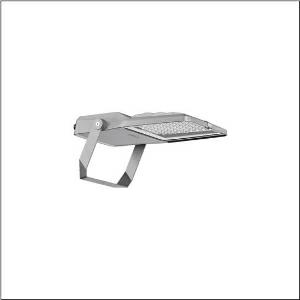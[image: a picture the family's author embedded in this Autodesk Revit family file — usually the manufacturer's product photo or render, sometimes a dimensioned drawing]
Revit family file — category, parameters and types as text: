
# Revit family: floodlight_fl_21_mini___pl43_5xa7775c2a1a_0644
name_source: partatom
category: Lighting Fixtures
units: mm (PartAtom-declared; Revit-internal decimal feet)

## family parameters
Cut with Voids When Loaded = No
Host = Face
Light Source = No
Part Type = Normal
Room Calculation Point = No
Round Connector Dimension = Use Diameter
Shared = No

## types (1)
- --- (1 x LED, 12500 lm, 89 W, 3000K)
    Apparent Load = 89 VA
    CIE Flux Codes = 27 78 99 100 100
    Color Rendering = 70
    Color Temperature = 3000K
    Default Elevation = 1800 mm
    Description = Floodlight FL 21 mini, floodlight, primary light control with lens, of PMMA, primary optical cover: protective disc, of toughened safety glass, transparent, light distribution: PL43, light emission: direct distribution, installation type: surface-mounted, LED, High Power LED, rated luminous flux: 12.500lm, luminous efficacy: 140lm/W, light colour: 730, colour temperature: 3000K, control gear: Smart Interface (Zhaga), control: flexible luminous flux parameterisation, time-dependent luminous flux control, constant luminous flux control, overheat protection, pre-setting: logarithmic dimming characteristic, with terminal, 6-pole, mains connection: 220..240V, AC, 50/60Hz, start of lifetime: 89W, end of service life: 94W, reduction: 43W, luminaire housing, of diecast aluminium, powder-coated, Siteco® metallic grey (DB 702S), corrosivity category C5 mid according to DIN EN ISO 12944, suitable for swimming pools, chlorine-resistant, sealing non-destructively replaceable, mounting bracket, of steel, galvanised, powder-coated, Siteco® metallic grey (DB 702S), Smart Interface above, protection rating (complete): IP66, insulation class (complete): insulation class II (safety insulation), certification: CE, ENEC, VDE, protection symbol: D, impact resistance: IK08, permissible operating ambient temperature: -40..+40°C, permissible operating ambient temperature for outdoor applications: -40..+50°C, standard: DIN EN 12944, LABS conformity tested according to VDMA 24364:2018-05, packaging unit: 1 piece

Light Distribution: PL43
    Height = 70 mm
    Lamp = 1 x LED
    Lamp Light Flux = 12500 lm
    Lamp Power = 89 W
    Lamp count = 1
    Length = 485 mm
    Luminous efficacy = 140 lm/W
    Manufacturer = Siteco
    ModVariant = No
    Model = 5XA7775C2A1A
    Number of Poles = 1
    OnlyDefault = Yes
    Power Factor = 1
    Product Name = Floodlight FL 21 mini | PL43
    Product group = floodlight | pylon annexe
    ProductGroupID = 6200
    Protection Class = Protection class II
    Protection Degree = IP 66
    RLX_Detail_Level = 1
    RLX_Emergency_Light_Flux = 0 lm
    RLX_Emergency_Type = 0
    RLX_Emergency_Type_DB = No
    RlxData = <blob elided: 95753 chars, md5=d74c3239>
    Socket = socket
    Standby Power = 0 W
    System Light Flux = 12500 lm
    System Power = 89 W
    Type Comments = factory setting: luminous flux: 100 % | dim-lin: 254 | 456 mA
    Type Image = l_1006845.jpg
    URL = http://relux.com
    VarID = @adj_161192
    Voltage = 0 V
    Weight = 0.00 kg
    Width = 337 mm

## geometry (parser evidence)
native form markers: Blend x4, Sweep x11
no freeform markers — native parametric forms only
